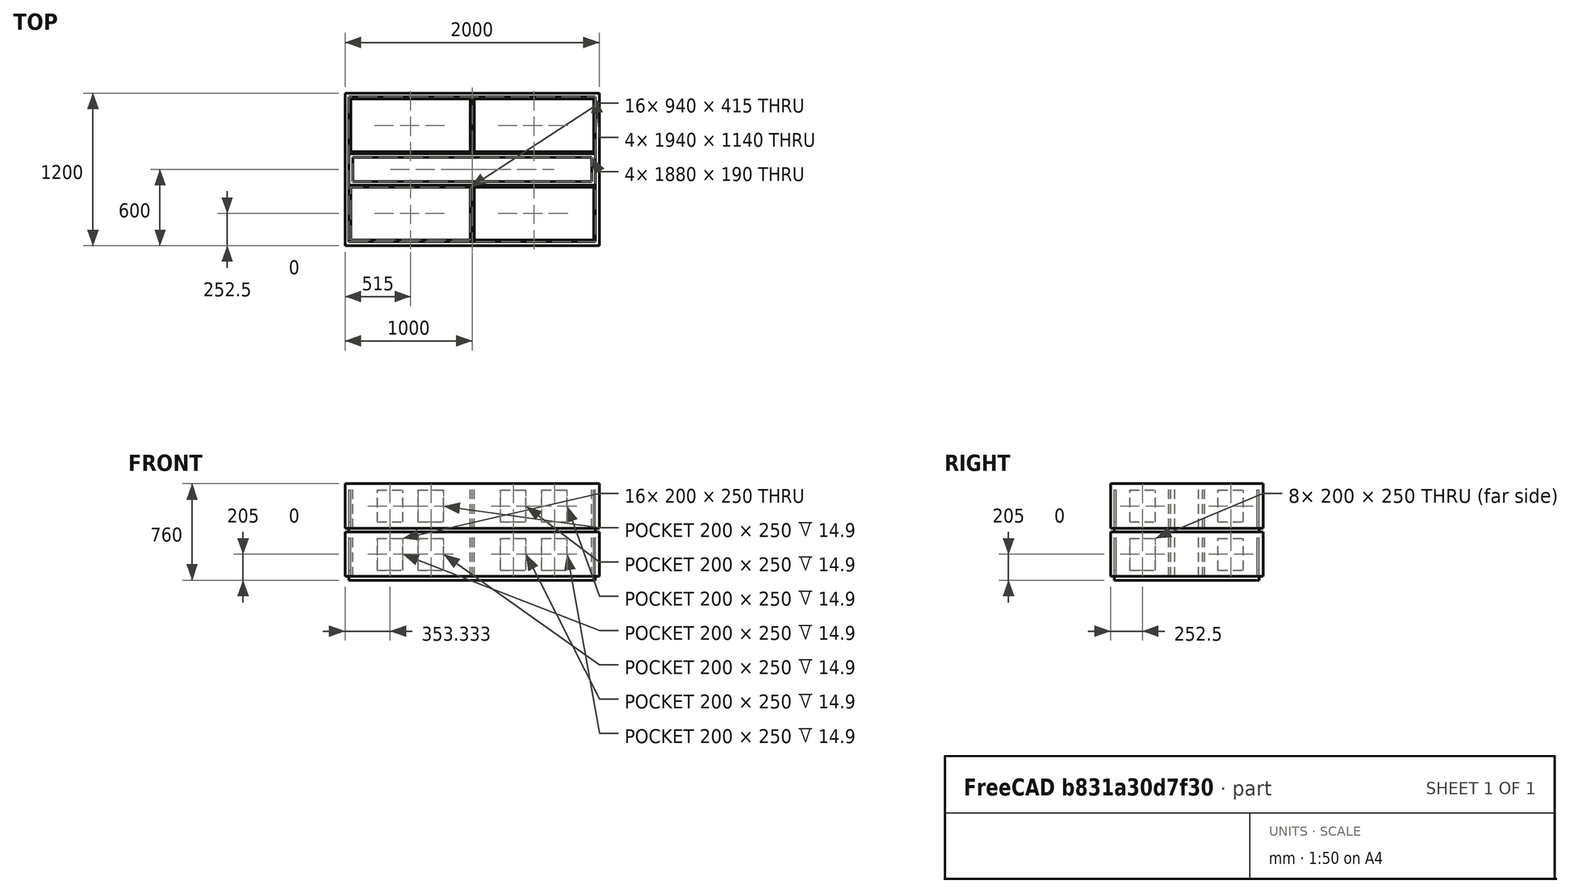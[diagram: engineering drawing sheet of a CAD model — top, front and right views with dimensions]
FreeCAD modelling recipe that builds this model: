
FCSTD DOCUMENT  (FreeCAD 1.0R39319 (Git))
Label: OfficeBuilding41_IFC1
License: All rights reserved
objects: Part::Feature×12, Part::FeaturePython×12, App::GeometryPython×2, Part::Box×2, Measure::MeasurePython×1, App::DocumentObjectGroup×1
note: 28 computed .brp shape members not serialized (recipe doc carries the construction recipe); baked Part::Feature solids carry a one-line shape summary decoded from their .brp

FEATURE [Part::Feature] Walls
  shape: bbox 2000 x 1200 x 350 mm, 10 faces (baked)
FEATURE [Part::Feature] Corridor  label="Corridor1"
  shape: bbox 1940 x 250 x 350 mm, 10 faces (baked)
FEATURE [Part::Feature] Office_1  label="офис 1.1"
  shape: bbox 970 x 445 x 350 mm, 25 faces (baked)
FEATURE [Part::Feature] Office_2  label="офис 1.2"
  shape: bbox 970 x 445 x 350 mm, 25 faces (baked)
FEATURE [Part::Feature] Office_3  label="офис 1.3"
  shape: bbox 970 x 445 x 350 mm, 25 faces (baked)
FEATURE [Part::Feature] Veranda
  shape: bbox 970 x 445 x 350 mm, 25 faces (baked)
FEATURE [App::GeometryPython] BuildingPart  label="1 этаж"  # Arch/BIM 10 (typed FeaturePython)
  Area = 0
  BuildingType = 0
  CompositionType = 0
  ElevationOfRefHeight = 0
  ElevationOfTerrain = 0
  GlobalId = 3dzsueIWH4v8jFkZjOCzj6
  Group = -> [Walls,Corridor,Office_1,Office_2,Office_3,Veranda]
  Height = 0
  HeightPropagate = true
  IfcData = IfcUID=3dzsueIWH4v8jFkZjOCzj6,+2 more (map truncated)
  IfcType = 10
  LevelOffset = 0
  LongName = Здание
  MaterialsTable = Undefined=0,1,2,3,4,5
  OnlySolids = true
FEATURE [Part::Feature] Walls001
  Placement = pos=(0,0,3.8) rot=(0,0,1;0rad)
  shape: bbox 2000 x 1200 x 350 mm, 10 faces (baked)
FEATURE [Part::Feature] Corridor001  label="Corridor2"
  Placement = pos=(0,0,3.8) rot=(0,0,1;0rad)
  shape: bbox 1940 x 250 x 350 mm, 10 faces (baked)
FEATURE [Part::Feature] Office_004  label="офис 2.1"
  Placement = pos=(0,0,3.8) rot=(0,0,1;0rad)
  shape: bbox 970 x 445 x 350 mm, 25 faces (baked)
FEATURE [Part::Feature] Office_005  label="офис 2.2"
  Placement = pos=(0,0,3.8) rot=(0,0,1;0rad)
  shape: bbox 970 x 445 x 350 mm, 25 faces (baked)
FEATURE [Part::Feature] Office_006  label="офис 2.3"
  Placement = pos=(0,0,3.8) rot=(0,0,1;0rad)
  shape: bbox 970 x 445 x 350 mm, 25 faces (baked)
FEATURE [Part::Feature] Veranda001  label="офис 2.4"
  Placement = pos=(0,0,3.8) rot=(0,0,1;0rad)
  shape: bbox 970 x 445 x 350 mm, 25 faces (baked)
FEATURE [App::GeometryPython] BuildingPart001  label="2 этаж"  # Arch/BIM 10 (typed FeaturePython)
  Area = 0
  BuildingType = 0
  CompositionType = 0
  ElevationOfRefHeight = 0
  ElevationOfTerrain = 0
  GlobalId = 2xffbW0LD5IQ51L3WXDfbp
  Group = -> [Walls001,Corridor001,Office_004,Office_005,Office_006,Veranda001]
  Height = 0
  HeightPropagate = true
  IfcData = IfcUID=2xffbW0LD5IQ51L3WXDfbp,+2 more (map truncated)
  IfcType = 10
  LevelOffset = 0
  LongName = Здание
  MaterialsTable = Undefined=0,1,2,3,4,5
  OnlySolids = true
  Placement = pos=(0,0,3.8) rot=(0,0,1;0rad)
FEATURE [Part::Box] Box  label="перекрытие1"
  AttacherType = Attacher::AttachEngine3D
  Height = 30
  Length = 1940
  Placement = pos=(30,30,-30) rot=(0,0,1;0rad)
  Width = 1140
FEATURE [Part::Box] Box001  label="перекрытие2"
  AttacherType = Attacher::AttachEngine3D
  Height = 30
  Length = 1940
  Placement = pos=(30,30,350) rot=(0,0,1;0rad)
  Width = 1140
FEATURE [Part::FeaturePython] Space  label="Офис 1.1"  # Arch/BIM 122 (typed FeaturePython)
  Area = 0
  AreaCalculationType = 0
  AutoPower = false
  Base = -> Office_1
  CompositionType = 0
  Conditioning = 0
  ElevationWithFlooring = 0
  EquipmentPower = 0
  FloorThickness = 0
  GlobalId = 0EompjOOjDh8OffYUslZAH
  HorizontalArea = 0
  IfcData = IfcUID=0EompjOOjDh8OffYUslZAH,+2 more (map truncated)
  IfcType = 122
  Internal = true
  LightingPower = 0
  LongName = офис 1.1
  MoveBase = false
  MoveWithHost = false
  NumberOfPeople = 0
  ObjectType = office
  PerimeterLength = 0
  PredefinedType = 0
  SpaceType = 0
  VerticalArea = 0
  expr: ElevationWithFlooring = .Shape.BoundBox.ZMin
FEATURE [Part::FeaturePython] Space001  label="Коридор 1"  # Arch/BIM 122 (typed FeaturePython)
  Area = 127800
  AreaCalculationType = 0
  AutoPower = false
  Base = -> Corridor
  CompositionType = 0
  Conditioning = 0
  ElevationWithFlooring = 0
  EquipmentPower = 0
  FloorThickness = 0
  GlobalId = 2mHXiWqG90ffk9KsE$WImU
  HorizontalArea = 127800
  IfcData = IfcUID=2mHXiWqG90ffk9KsE$WImU,+2 more (map truncated)
  IfcType = 122
  Internal = true
  LightingPower = 0
  LongName = Коридор 1
  MoveBase = false
  MoveWithHost = false
  NumberOfPeople = 0
  ObjectType = Corridor
  PerimeterLength = 8520
  PredefinedType = 0
  SpaceType = 0
  VerticalArea = 2982000
  expr: ElevationWithFlooring = .Shape.BoundBox.ZMin
FEATURE [Part::FeaturePython] Space002  label="Офис 1.2"  # Arch/BIM 122 (typed FeaturePython)
  Area = 0
  AreaCalculationType = 0
  AutoPower = false
  Base = -> Office_2
  CompositionType = 0
  Conditioning = 0
  ElevationWithFlooring = 0
  EquipmentPower = 0
  FloorThickness = 0
  GlobalId = 3aJg43ji9BCRf_Pv0$KAyr
  HorizontalArea = 0
  IfcData = IfcUID=3aJg43ji9BCRf_Pv0$KAyr,+2 more (map truncated)
  IfcType = 122
  Internal = true
  LightingPower = 0
  LongName = офис 1.2
  MoveBase = false
  MoveWithHost = false
  NumberOfPeople = 0
  ObjectType = office
  PerimeterLength = 0
  PredefinedType = 0
  SpaceType = 0
  VerticalArea = 0
  expr: ElevationWithFlooring = .Shape.BoundBox.ZMin
FEATURE [Part::FeaturePython] Space003  label="Офис 1.3"  # Arch/BIM 122 (typed FeaturePython)
  Area = 0
  AreaCalculationType = 0
  AutoPower = false
  Base = -> Office_3
  CompositionType = 0
  Conditioning = 0
  ElevationWithFlooring = 0
  EquipmentPower = 0
  FloorThickness = 0
  GlobalId = 1sX2viaiPA_gy58ZIuCBqU
  HorizontalArea = 0
  IfcData = IfcUID=1sX2viaiPA_gy58ZIuCBqU,+2 more (map truncated)
  IfcType = 122
  Internal = true
  LightingPower = 0
  LongName = офис 1.3
  MoveBase = false
  MoveWithHost = false
  NumberOfPeople = 0
  ObjectType = office
  PerimeterLength = 0
  PredefinedType = 0
  SpaceType = 0
  VerticalArea = 0
  expr: ElevationWithFlooring = .Shape.BoundBox.ZMin
FEATURE [Part::FeaturePython] Space004  label="Веранда"  # Arch/BIM 122 (typed FeaturePython)
  Area = 0
  AreaCalculationType = 0
  AutoPower = false
  Base = -> Veranda
  CompositionType = 0
  Conditioning = 0
  ElevationWithFlooring = 0
  EquipmentPower = 0
  FloorThickness = 0
  GlobalId = 0MQPC_Au5AEw6FOCvTkluY
  HorizontalArea = 0
  IfcData = IfcUID=0MQPC_Au5AEw6FOCvTkluY,+2 more (map truncated)
  IfcType = 122
  Internal = true
  LightingPower = 0
  LongName = Веранда
  MoveBase = false
  MoveWithHost = false
  NumberOfPeople = 0
  ObjectType = veranda
  PerimeterLength = 0
  PredefinedType = 0
  SpaceType = 0
  VerticalArea = 0
  expr: ElevationWithFlooring = .Shape.BoundBox.ZMin
FEATURE [Part::FeaturePython] Space005  label="Корридор 2"  # Arch/BIM 122 (typed FeaturePython)
  Area = 127800
  AreaCalculationType = 0
  AutoPower = false
  Base = -> Corridor001
  CompositionType = 0
  Conditioning = 0
  ElevationWithFlooring = 380
  EquipmentPower = 0
  FloorThickness = 0
  GlobalId = 1M8vFcEXT7we4$IuSu4Sf5
  HorizontalArea = 127800
  IfcData = IfcUID=1M8vFcEXT7we4$IuSu4Sf5,+2 more (map truncated)
  IfcType = 122
  Internal = true
  LightingPower = 0
  LongName = Коридор 2
  MoveBase = false
  MoveWithHost = false
  NumberOfPeople = 0
  ObjectType = Corridor
  PerimeterLength = 8520
  PredefinedType = 0
  SpaceType = 0
  VerticalArea = 2982000
  expr: ElevationWithFlooring = .Shape.BoundBox.ZMin
FEATURE [Part::FeaturePython] Space006  label="Офис 2.1"  # Arch/BIM 122 (typed FeaturePython)
  Area = 0
  AreaCalculationType = 0
  AutoPower = false
  Base = -> Office_004
  CompositionType = 0
  Conditioning = 0
  ElevationWithFlooring = 380
  EquipmentPower = 0
  FloorThickness = 0
  GlobalId = 3ZVceRlq9A6f946qSKD264
  HorizontalArea = 0
  IfcData = IfcUID=3ZVceRlq9A6f946qSKD264,+2 more (map truncated)
  IfcType = 122
  Internal = true
  LightingPower = 0
  LongName = офис 2.1
  MoveBase = false
  MoveWithHost = false
  NumberOfPeople = 0
  ObjectType = office
  PerimeterLength = 0
  PredefinedType = 0
  SpaceType = 0
  VerticalArea = 0
  expr: ElevationWithFlooring = .Shape.BoundBox.ZMin
FEATURE [Part::FeaturePython] Space007  label="Офис 2.2"  # Arch/BIM 122 (typed FeaturePython)
  Area = 0
  AreaCalculationType = 0
  AutoPower = false
  Base = -> Office_005
  CompositionType = 0
  Conditioning = 0
  ElevationWithFlooring = 380
  EquipmentPower = 0
  FloorThickness = 0
  GlobalId = 064dDzFizByRmIoVy8F59G
  HorizontalArea = 0
  IfcData = IfcUID=064dDzFizByRmIoVy8F59G,+2 more (map truncated)
  IfcType = 122
  Internal = true
  LightingPower = 0
  LongName = офис 2.2
  MoveBase = false
  MoveWithHost = false
  NumberOfPeople = 0
  ObjectType = office
  PerimeterLength = 0
  PredefinedType = 0
  SpaceType = 0
  VerticalArea = 0
  expr: ElevationWithFlooring = .Shape.BoundBox.ZMin
FEATURE [Part::FeaturePython] Space008  label="Офис 2.3"  # Arch/BIM 122 (typed FeaturePython)
  Area = 0
  AreaCalculationType = 0
  AutoPower = false
  Base = -> Office_006
  CompositionType = 0
  Conditioning = 0
  ElevationWithFlooring = 380
  EquipmentPower = 0
  FloorThickness = 0
  GlobalId = 2VrTc8Bw19nA3YtTmF05up
  HorizontalArea = 0
  IfcData = IfcUID=2VrTc8Bw19nA3YtTmF05up,+2 more (map truncated)
  IfcType = 122
  Internal = true
  LightingPower = 0
  LongName = офис 2.3
  MoveBase = false
  MoveWithHost = false
  NumberOfPeople = 0
  ObjectType = office
  PerimeterLength = 0
  PredefinedType = 0
  SpaceType = 0
  VerticalArea = 0
  expr: ElevationWithFlooring = .Shape.BoundBox.ZMin
FEATURE [Part::FeaturePython] Space009  label="Офис 2.4"  # Arch/BIM 122 (typed FeaturePython)
  Area = 0
  AreaCalculationType = 0
  AutoPower = false
  Base = -> Veranda001
  CompositionType = 0
  Conditioning = 0
  ElevationWithFlooring = 380
  EquipmentPower = 0
  FloorThickness = 0
  GlobalId = 2vGEnyzEHDSeFIrJ$DGSo3
  HorizontalArea = 0
  IfcData = IfcUID=2vGEnyzEHDSeFIrJ$DGSo3,+2 more (map truncated)
  IfcType = 122
  Internal = true
  LightingPower = 0
  LongName = офис 2.4
  MoveBase = false
  MoveWithHost = false
  NumberOfPeople = 0
  ObjectType = office
  PerimeterLength = 0
  PredefinedType = 0
  SpaceType = 0
  VerticalArea = 0
  expr: ElevationWithFlooring = .Shape.BoundBox.ZMin
FEATURE [Part::FeaturePython] Space010  label="Перекрытие1"  # Arch/BIM 122 (typed FeaturePython)
  Area = 2211600
  AreaCalculationType = 0
  AutoPower = false
  Base = -> Box
  CompositionType = 0
  Conditioning = 0
  ElevationWithFlooring = -30
  EquipmentPower = 0
  FloorThickness = 0
  GlobalId = 0ak6SHlsb4Evv$HGMoQG6l
  HorizontalArea = 2211600
  IfcData = IfcUID=0ak6SHlsb4Evv$HGMoQG6l,+2 more (map truncated)
  IfcType = 122
  Internal = true
  LightingPower = 0
  LongName = перекрытие1
  MoveBase = false
  MoveWithHost = false
  NumberOfPeople = 0
  ObjectType = perekrytie
  PerimeterLength = 6160
  PredefinedType = 0
  SpaceType = 0
  VerticalArea = 184800
  expr: ElevationWithFlooring = .Shape.BoundBox.ZMin
FEATURE [Part::FeaturePython] Space011  label="Перекрытие2"  # Arch/BIM 122 (typed FeaturePython)
  Area = 2211600
  AreaCalculationType = 0
  AutoPower = false
  Base = -> Box001
  CompositionType = 0
  Conditioning = 0
  ElevationWithFlooring = 350
  EquipmentPower = 0
  FloorThickness = 0
  GlobalId = 1oEOx9iWf6DhE3TyzSqNrx
  HorizontalArea = 2211600
  IfcData = IfcUID=1oEOx9iWf6DhE3TyzSqNrx,+2 more (map truncated)
  IfcType = 122
  Internal = true
  LightingPower = 0
  LongName = перекрытие2
  MoveBase = false
  MoveWithHost = false
  NumberOfPeople = 0
  ObjectType = perekrytie
  PerimeterLength = 6160
  PredefinedType = 0
  SpaceType = 0
  VerticalArea = 184800
  expr: ElevationWithFlooring = .Shape.BoundBox.ZMin
FEATURE [Measure::MeasurePython] Center_of_Mass  label="Center_of_Mass: COM
X: 543,91 mm
Y: 278,53 mm
Z: 555,00 mm"  # WARN: FeaturePython — macro-defined, semantics opaque (R4)
  Element = -> Space006
  Placement = pos=(543.907,278.535,555) rot=(0,0,1;0rad)
  Result = (543.907,278.535,555)
FEATURE [App::DocumentObjectGroup] Measurements
  Group = -> [Center_of_Mass]
